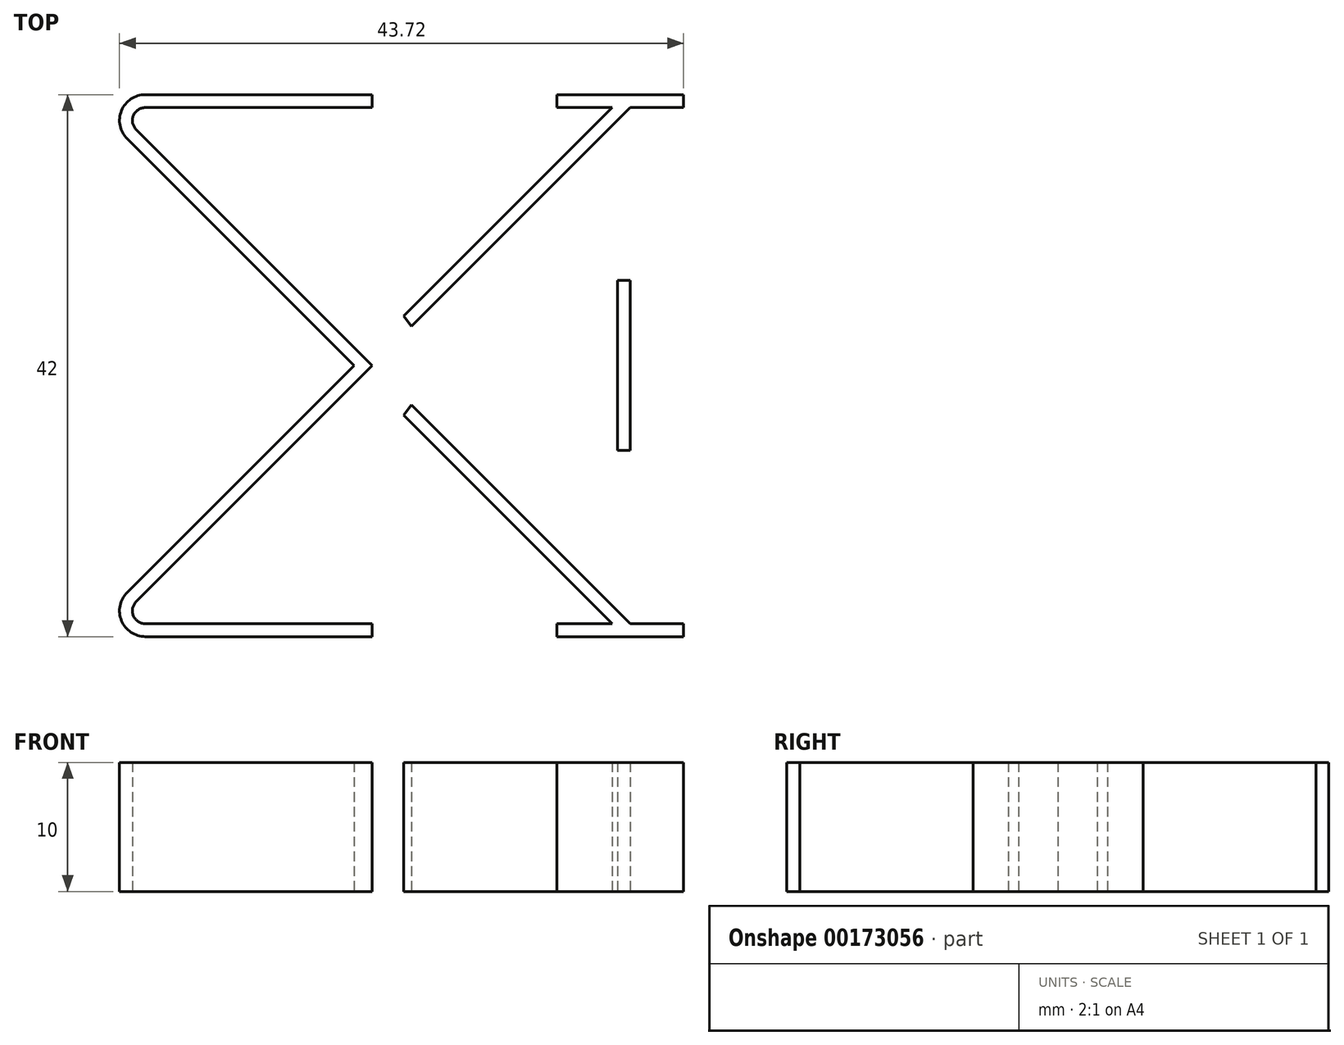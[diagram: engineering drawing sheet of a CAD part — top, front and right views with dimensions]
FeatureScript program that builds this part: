
annotation { "Feature Type Name" : "Feature", "Feature Type Description" : "" }
export const myFeature = defineFeature(function(context is Context, id is Id, definition is map)
    precondition{}
    {
        {
            var Q0;
            Q0=qCreatedBy(makeId("Top.planeOp"),FACE);
            var sketch = newSketch(context, id + "F0", { "sketchPlane" : qUnion([Q0])});
            skLineSegment(sketch, "E0.left", {"start": v(20, 6.62) * mm, "end": v(20, -6.55) * mm});
            skPoint(sketch, "E0.middle", {"position": v(0, 0) * mm});
            skLineSegment(sketch, "E1", {"start": v(-18.3, -18.3) * mm, "end": v(0, 0) * mm});
            skLineSegment(sketch, "E2", {"start": v(-18.3, 18.3) * mm, "end": v(0, 0) * mm});
            skLineSegment(sketch, "E3.trimOffspring", {"start": v(0, 20) * mm, "end": v(-17.59, 20) * mm});
            skLineSegment(sketch, "E4.trimOffspring", {"start": v(3.05, 3.05) * mm, "end": v(20, 20) * mm});
            skLineSegment(sketch, "E5.trimOffspring", {"start": v(3.05, -3.05) * mm, "end": v(20, -20) * mm});
            skPoint(sketch, "E6.orphan", {"position": v(0, -20) * mm});
            skLineSegment(sketch, "E7.trimOffspring", {"start": v(0, -20) * mm, "end": v(-17.59, -20) * mm});
            skPoint(sketch, "E0.bottom.end.orphan", {"position": v(8.13, 20) * mm});
            skPoint(sketch, "E8.visualSharp", {"position": v(-20, 20) * mm});
            skArc(sketch, "E8.filletArc", {"start": v(-17.59, 20) * mm, "mid": v(-18.5, 19.38) * mm, "end": v(-18.3, 18.3) * mm});
            skPoint(sketch, "E9.visualSharp", {"position": v(-20, -20) * mm});
            skArc(sketch, "E9.filletArc", {"start": v(-18.3, -18.3) * mm, "mid": v(-18.5, -19.38) * mm, "end": v(-17.59, -20) * mm});
            skLineSegment(sketch, "E10.0", {"start": v(0, -21) * mm, "end": v(-17.59, -21) * mm});
            skArc(sketch, "E10.1", {"start": v(-19, -17.59) * mm, "mid": v(-19.43, -19.77) * mm, "end": v(-17.59, -21) * mm});
            skLineSegment(sketch, "E10.2", {"start": v(0, 21) * mm, "end": v(-17.59, 21) * mm});
            skArc(sketch, "E10.3", {"start": v(-17.59, 21) * mm, "mid": v(-19.43, 19.77) * mm, "end": v(-19, 17.59) * mm});
            skLineSegment(sketch, "E10.4", {"start": v(-19, 17.59) * mm, "end": v(-1.41, 0) * mm});
            skLineSegment(sketch, "E10.5", {"start": v(-19, -17.59) * mm, "end": v(-1.41, 0) * mm});
            skLineSegment(sketch, "E11.0", {"start": v(2.42, 3.84) * mm, "end": v(18.59, 20) * mm});
            skLineSegment(sketch, "E12.0", {"start": v(2.42, -3.84) * mm, "end": v(18.59, -20) * mm});
            skLineSegment(sketch, "E13.0", {"start": v(19, 6.62) * mm, "end": v(19, -6.55) * mm});
            skLineSegment(sketch, "E14", {"start": v(0, 20) * mm, "end": v(0, 21) * mm});
            skLineSegment(sketch, "E15", {"start": v(2.42, 3.84) * mm, "end": v(3.05, 3.05) * mm});
            skLineSegment(sketch, "E16", {"start": v(2.42, -3.84) * mm, "end": v(3.05, -3.05) * mm});
            skLineSegment(sketch, "E17", {"start": v(19, -6.55) * mm, "end": v(20, -6.55) * mm});
            skLineSegment(sketch, "E18", {"start": v(20, 6.62) * mm, "end": v(19, 6.62) * mm});
            skLineSegment(sketch, "E19", {"start": v(0, -20) * mm, "end": v(0, -21) * mm});
            skLineSegment(sketch, "E20", {"start": v(19.59, 21) * mm, "end": v(14.3, 21) * mm});
            skLineSegment(sketch, "E21", {"start": v(18.59, 20) * mm, "end": v(14.3, 20) * mm});
            skLineSegment(sketch, "E22", {"start": v(14.3, 20) * mm, "end": v(14.3, 21) * mm});
            skLineSegment(sketch, "E23", {"start": v(19.59, 21) * mm, "end": v(24.13, 21) * mm});
            skLineSegment(sketch, "E24", {"start": v(24.13, 21) * mm, "end": v(24.13, 20) * mm});
            skLineSegment(sketch, "E25", {"start": v(24.13, 20) * mm, "end": v(20, 20) * mm});
            skLineSegment(sketch, "E26", {"start": v(0, 0) * mm, "end": v(11.43, 0) * mm, "construction": true});
            skLineSegment(sketch, "E27.MirrorCS", {"start": v(24.13, -20) * mm, "end": v(20, -20) * mm});
            skLineSegment(sketch, "E28.MirrorCS", {"start": v(19.59, -21) * mm, "end": v(14.3, -21) * mm});
            skLineSegment(sketch, "E29.MirrorCS", {"start": v(19.59, -21) * mm, "end": v(24.13, -21) * mm});
            skLineSegment(sketch, "E30.MirrorCS", {"start": v(24.13, -21) * mm, "end": v(24.13, -20) * mm});
            skLineSegment(sketch, "E31.MirrorCS", {"start": v(14.3, -20) * mm, "end": v(14.3, -21) * mm});
            skLineSegment(sketch, "E32.MirrorCS", {"start": v(18.59, -20) * mm, "end": v(14.3, -20) * mm});
            skLineSegment(sketch, "E33.bottom", {"start": v(-20, -21) * mm, "end": v(20, -21) * mm, "construction": true});
            skLineSegment(sketch, "E33.top", {"start": v(-20, 21) * mm, "end": v(20, 21) * mm, "construction": true});
            skLineSegment(sketch, "E33.left", {"start": v(-20, -21) * mm, "end": v(-20, 21) * mm, "construction": true});
            skLineSegment(sketch, "E33.right", {"start": v(20, -21) * mm, "end": v(20, 21) * mm, "construction": true});
            skPoint(sketch, "E34.orphan", {"position": v(20, -20) * mm});
            skSolve(sketch);
        }
        {
            var Q0;
            Q0 = qSketchRegion(id + "F0", true);
            extrude(context, id + "F1", {"entities" : qUnion([Q0]), "depth" : 10 * mm});
        }
    });
